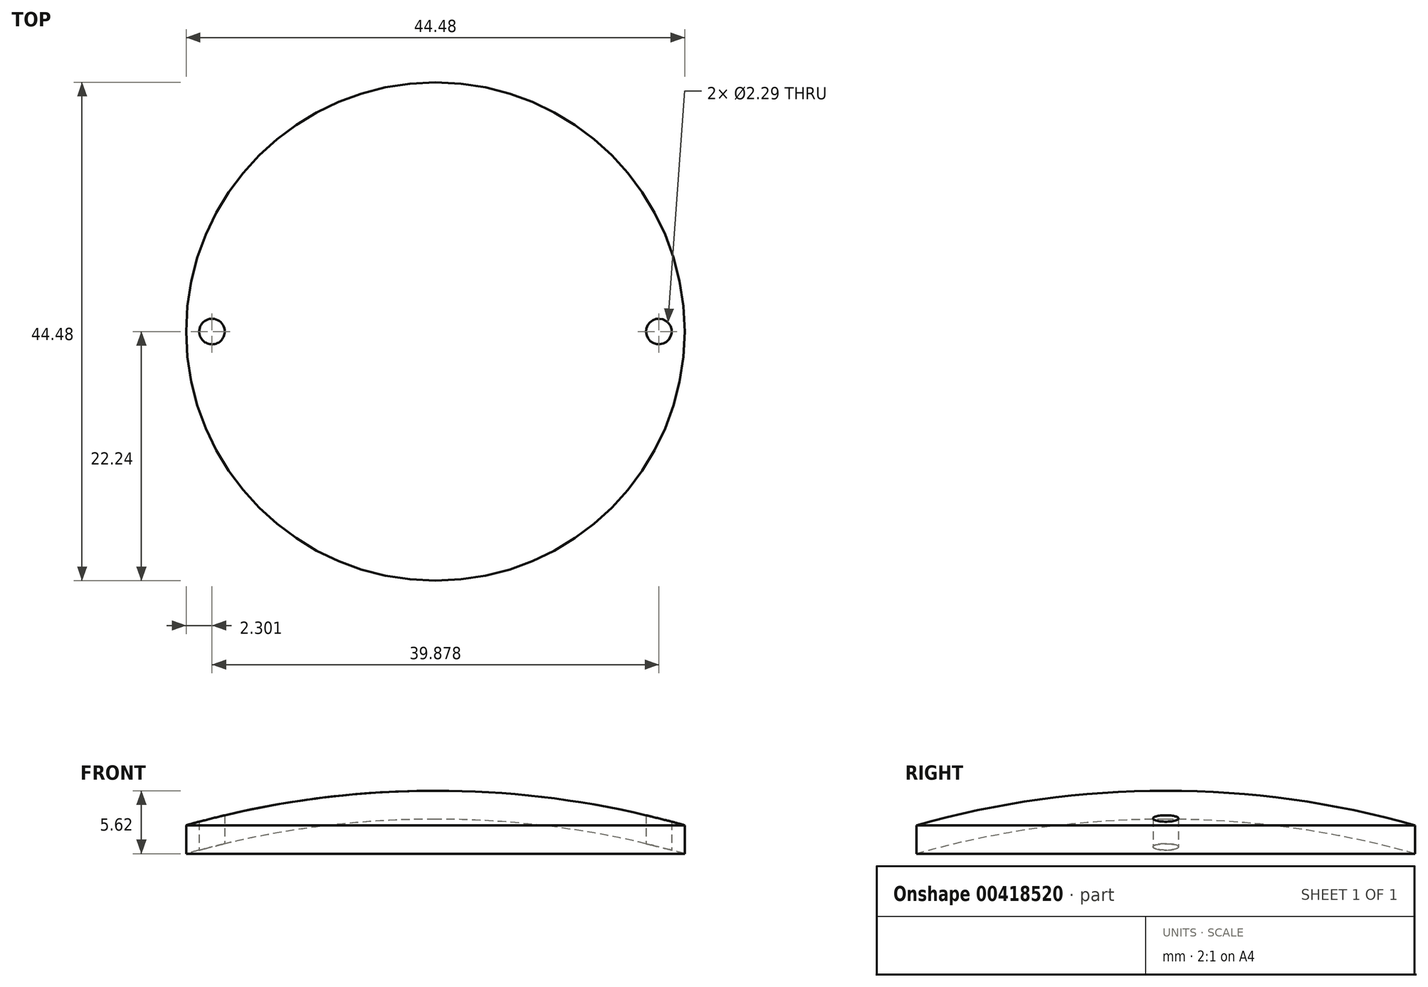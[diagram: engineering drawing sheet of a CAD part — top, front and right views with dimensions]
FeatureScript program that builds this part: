
annotation { "Feature Type Name" : "Feature", "Feature Type Description" : "" }
export const myFeature = defineFeature(function(context is Context, id is Id, definition is map)
    precondition{}
    {
        {
            var Q0;
            Q0=qCreatedBy(makeId("Top.planeOp"),FACE);
            var sketch = newSketch(context, id + "F0", { "sketchPlane" : qUnion([Q0])});
            skCircle(sketch, "E0", {"center": v(0, 0) * mm, "radius": 22.23 * mm});
            skCircle(sketch, "E1", {"center": v(0, 0) * mm, "radius": 22.99 * mm});
            skCircle(sketch, "E2", {"center": v(-19.94, 0) * mm, "radius": 1.14 * mm});
            skCircle(sketch, "E3", {"center": v(19.94, 0) * mm, "radius": 1.14 * mm});
            skSolve(sketch);
        }
        {
            var Q0;
            Q0=qCreatedBy(makeId("Front.planeOp"),FACE);
            var sketch = newSketch(context, id + "F1", { "sketchPlane" : qUnion([Q0])});
            skLineSegment(sketch, "E4", {"start": v(-37.44, 2.54) * mm, "end": v(37.44, 2.54) * mm, "construction": true});
            skLineSegment(sketch, "E5", {"start": v(-37.44, 5.08) * mm, "end": v(37.44, 5.08) * mm, "construction": true});
            skPoint(sketch, "E6.startSnap0", {"position": v(0, 5.08) * mm});
            skLineSegment(sketch, "E7", {"start": v(-9.06, -76.2) * mm, "end": v(8.35, -76.2) * mm, "construction": true});
            skLineSegment(sketch, "E8", {"start": v(-9.06, -78.74) * mm, "end": v(8.35, -78.74) * mm, "construction": true});
            skLineSegment(sketch, "E9", {"start": v(0, -67.75) * mm, "end": v(0, -86.32) * mm, "construction": true});
            skLineSegment(sketch, "E10", {"start": v(-22.24, 0) * mm, "end": v(-22.24, 2.54) * mm});
            skArc(sketch, "E11", {"start": v(-22.24, 0) * mm, "mid": v(-11.23, 2.3) * mm, "end": v(0, 3.08) * mm});
            skArc(sketch, "E12", {"start": v(-22.24, 2.54) * mm, "mid": v(-11.23, 4.85) * mm, "end": v(0, 5.62) * mm});
            skLineSegment(sketch, "E13", {"start": v(0, 3.08) * mm, "end": v(0, 5.62) * mm});
            skSolve(sketch);
        }
        {
            var Q0;
            Q0=makeQuery(id+"F1.imprint","IMPRINT",FACE,{"disambiguationData":[TD([[makeQuery(id+"F1.imprint","IMPRINT",EDGE,{"derivedFrom":sQuery(id+"F1.wireOp",EDGE,"E10")}),-1.0]])]});
            var Q1;
            Q1=sQuery(id+"F1.wireOp",EDGE,"E13");
            revolve(context, id + "F2", {"entities" : qUnion([Q0]), "axis" : qUnion([Q1]), "revolveType" : RevolveType.FULL});
        }
        {
            var Q0;
            Q0=makeQuery(id+"F0.imprint","IMPRINT",FACE,{"disambiguationData":[TD([[makeQuery(id+"F0.imprint","IMPRINT",EDGE,{"derivedFrom":sQuery(id+"F0.wireOp",EDGE,"E2")}),1.0]])]});
            var Q1;
            Q1=makeQuery(id+"F0.imprint","IMPRINT",FACE,{"disambiguationData":[TD([[makeQuery(id+"F0.imprint","IMPRINT",EDGE,{"derivedFrom":sQuery(id+"F0.wireOp",EDGE,"E3")}),1.0]])]});
            extrude(context, id + "F3", {"entities" : qUnion([Q0, Q1]), "operationType" : NewBodyOperationType.REMOVE, "endBound" : BoundingType.THROUGH_ALL, "depth" : 25.4 * mm, "offsetDistance" : 25.4 * mm});
        }
    });
